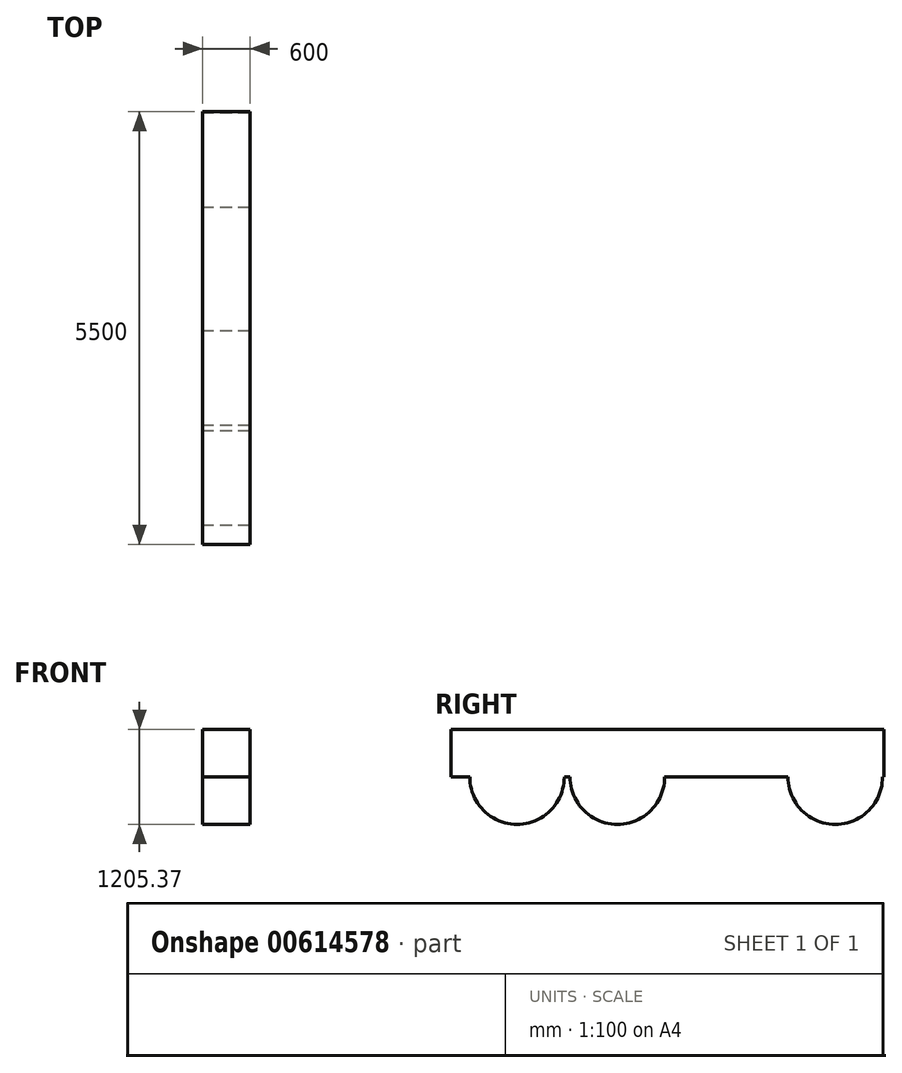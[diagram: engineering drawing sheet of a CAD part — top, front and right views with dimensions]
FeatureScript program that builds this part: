
annotation { "Feature Type Name" : "Feature", "Feature Type Description" : "" }
export const myFeature = defineFeature(function(context is Context, id is Id, definition is map)
    precondition{}
    {
        {
            var Q0;
            Q0=qCreatedBy(makeId("Right.planeOp"),FACE);
            var sketch = newSketch(context, id + "F0", { "sketchPlane" : qUnion([Q0])});
            skCircle(sketch, "E0", {"center": v(2042.1, 0) * mm, "radius": 600 * mm});
            skCircle(sketch, "E1", {"center": v(-2000.51, 0) * mm, "radius": 600 * mm});
            skCircle(sketch, "E2", {"center": v(-725.82, 0) * mm, "radius": 600 * mm});
            skLineSegment(sketch, "E3.bottom", {"start": v(-2839.63, 605.37) * mm, "end": v(2660.37, 605.37) * mm});
            skLineSegment(sketch, "E3.top", {"start": v(-2839.63, 5.37) * mm, "end": v(2660.37, 5.37) * mm});
            skLineSegment(sketch, "E3.left", {"start": v(-2839.63, 605.37) * mm, "end": v(-2839.63, 5.37) * mm});
            skLineSegment(sketch, "E3.right", {"start": v(2660.37, 605.37) * mm, "end": v(2660.37, 5.37) * mm});
            skPoint(sketch, "E3.middle", {"position": v(-89.63, 305.37) * mm});
            skSolve(sketch);
        }
        {
            var Q0;
            {var subQ0=sQuery(id+"F0.wireOp",EDGE,"E3.top");var subQ1=sQuery(id+"F0.wireOp",EDGE,"E1");var subQ2=makeQuery(id+"F0.imprint","INTERSECT",VERTEX,{"disambiguationData":[OD(0.0)],"derivedFrom":[subQ1,subQ0]});Q0=makeQuery(id+"F0.imprint","IMPRINT",FACE,{"disambiguationData":[TD([[makeQuery(id+"F0.imprint","IMPRINT",EDGE,{"disambiguationData":[TD([[subQ2,-1.0]])],"derivedFrom":subQ1}),1.0]])]});}
            var Q1;
            {var subQ0=sQuery(id+"F0.wireOp",EDGE,"E3.top");var subQ1=sQuery(id+"F0.wireOp",EDGE,"E1");var subQ2=makeQuery(id+"F0.imprint","INTERSECT",VERTEX,{"disambiguationData":[OD(0.0)],"derivedFrom":[subQ1,subQ0]});Q1=makeQuery(id+"F0.imprint","IMPRINT",FACE,{"disambiguationData":[TD([[makeQuery(id+"F0.imprint","IMPRINT",EDGE,{"disambiguationData":[TD([[subQ2,1.0]])],"derivedFrom":subQ1}),1.0]])]});}
            var Q2;
            Q2=makeQuery(id+"F0.imprint","IMPRINT",FACE,{"disambiguationData":[TD([[makeQuery(id+"F0.imprint","IMPRINT",EDGE,{"derivedFrom":sQuery(id+"F0.wireOp",EDGE,"E3.bottom")}),-1.0]])]});
            var Q3;
            {var subQ0=sQuery(id+"F0.wireOp",EDGE,"E3.top");var subQ1=sQuery(id+"F0.wireOp",EDGE,"E2");var subQ2=makeQuery(id+"F0.imprint","INTERSECT",VERTEX,{"disambiguationData":[OD(0.0)],"derivedFrom":[subQ1,subQ0]});Q3=makeQuery(id+"F0.imprint","IMPRINT",FACE,{"disambiguationData":[TD([[makeQuery(id+"F0.imprint","IMPRINT",EDGE,{"disambiguationData":[TD([[subQ2,-1.0]])],"derivedFrom":subQ1}),1.0]])]});}
            var Q4;
            {var subQ0=sQuery(id+"F0.wireOp",EDGE,"E3.top");var subQ1=sQuery(id+"F0.wireOp",EDGE,"E2");var subQ2=makeQuery(id+"F0.imprint","INTERSECT",VERTEX,{"disambiguationData":[OD(0.0)],"derivedFrom":[subQ1,subQ0]});Q4=makeQuery(id+"F0.imprint","IMPRINT",FACE,{"disambiguationData":[TD([[makeQuery(id+"F0.imprint","IMPRINT",EDGE,{"disambiguationData":[TD([[subQ2,1.0]])],"derivedFrom":subQ1}),1.0]])]});}
            var Q5;
            {var subQ0=sQuery(id+"F0.wireOp",EDGE,"E3.top");var subQ1=sQuery(id+"F0.wireOp",EDGE,"E0");var subQ2=makeQuery(id+"F0.imprint","INTERSECT",VERTEX,{"disambiguationData":[OD(0.0)],"derivedFrom":[subQ1,subQ0]});Q5=makeQuery(id+"F0.imprint","IMPRINT",FACE,{"disambiguationData":[TD([[makeQuery(id+"F0.imprint","IMPRINT",EDGE,{"disambiguationData":[TD([[subQ2,-1.0]])],"derivedFrom":subQ1}),1.0]])]});}
            var Q6;
            {var subQ0=sQuery(id+"F0.wireOp",EDGE,"E3.top");var subQ1=sQuery(id+"F0.wireOp",EDGE,"E0");var subQ2=makeQuery(id+"F0.imprint","INTERSECT",VERTEX,{"disambiguationData":[OD(0.0)],"derivedFrom":[subQ1,subQ0]});Q6=makeQuery(id+"F0.imprint","IMPRINT",FACE,{"disambiguationData":[TD([[makeQuery(id+"F0.imprint","IMPRINT",EDGE,{"disambiguationData":[TD([[subQ2,1.0]])],"derivedFrom":subQ1}),1.0]])]});}
            extrude(context, id + "F1", {"entities" : qUnion([Q0, Q1, Q2, Q3, Q4, Q5, Q6]), "depth" : 600 * mm, "offsetDistance" : 25 * mm});
        }
    });
